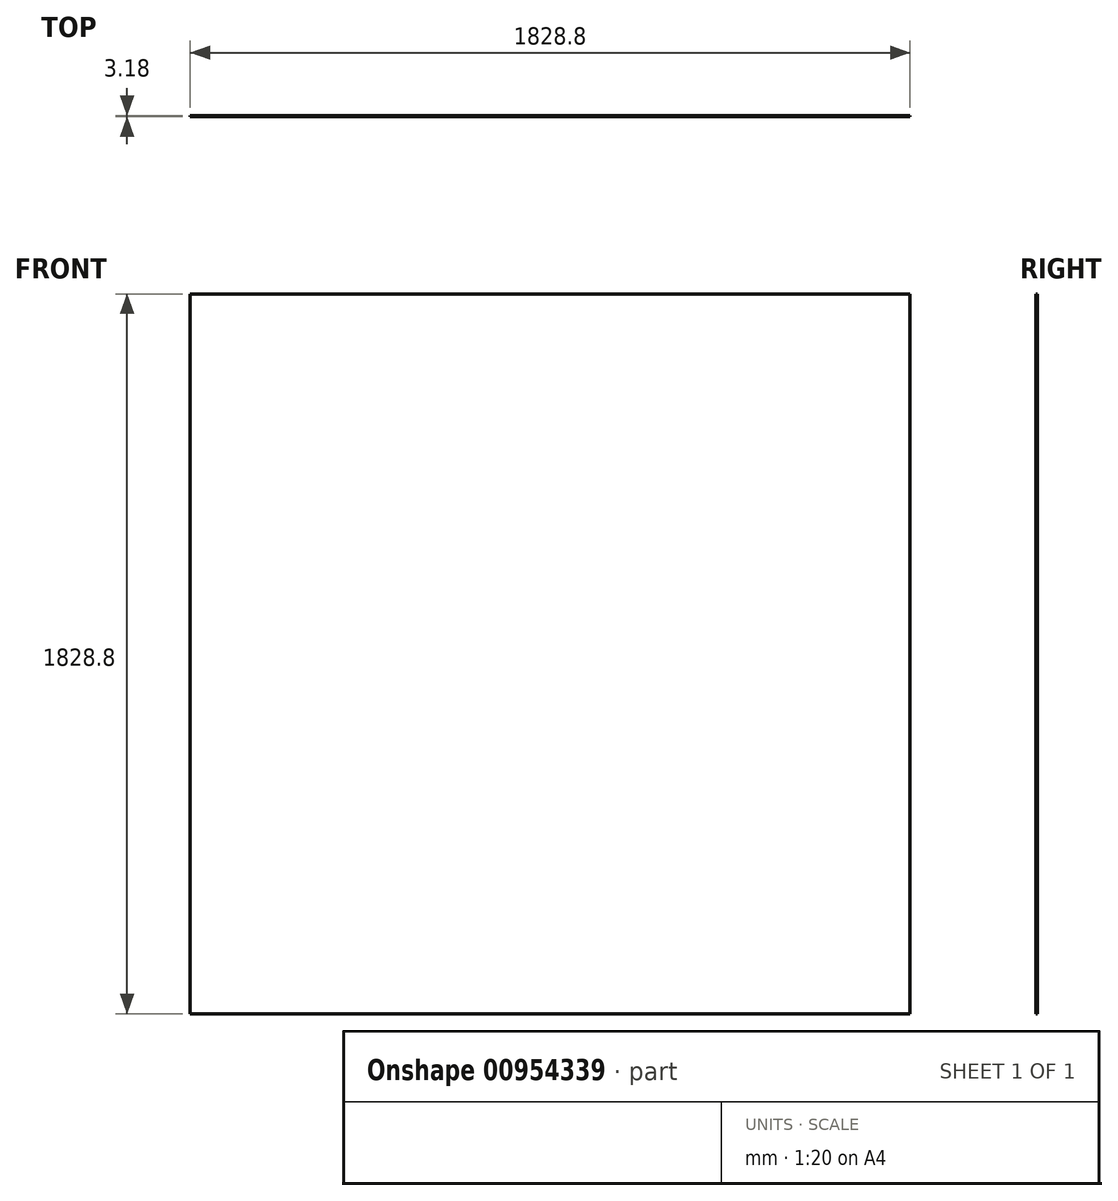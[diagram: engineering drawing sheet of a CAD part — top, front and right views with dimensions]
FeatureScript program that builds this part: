
annotation { "Feature Type Name" : "Feature", "Feature Type Description" : "" }
export const myFeature = defineFeature(function(context is Context, id is Id, definition is map)
    precondition{}
    {
        {
            var Q0;
            Q0=qCreatedBy(makeId("Front.planeOp"),FACE);
            var sketch = newSketch(context, id + "F0", { "sketchPlane" : qUnion([Q0])});
            skLineSegment(sketch, "E0.bottom", {"start": v(-862.42, 910.58) * mm, "end": v(-2691.22, 910.58) * mm});
            skLineSegment(sketch, "E0.top", {"start": v(-862.42, -918.22) * mm, "end": v(-2691.22, -918.22) * mm});
            skLineSegment(sketch, "E0.left", {"start": v(-862.42, 910.58) * mm, "end": v(-862.42, -918.22) * mm});
            skLineSegment(sketch, "E0.right", {"start": v(-2691.22, 910.58) * mm, "end": v(-2691.22, -918.22) * mm});
            skPoint(sketch, "E0.middle", {"position": v(-1776.82, -3.82) * mm});
            skSolve(sketch);
        }
        {
            var Q0;
            Q0 = qSketchRegion(id + "F0", true);
            extrude(context, id + "F1", {"entities" : qUnion([Q0]), "depth" : 3.17 * mm, "offsetDistance" : 25.4 * mm, "symmetric" : true});
        }
    });
